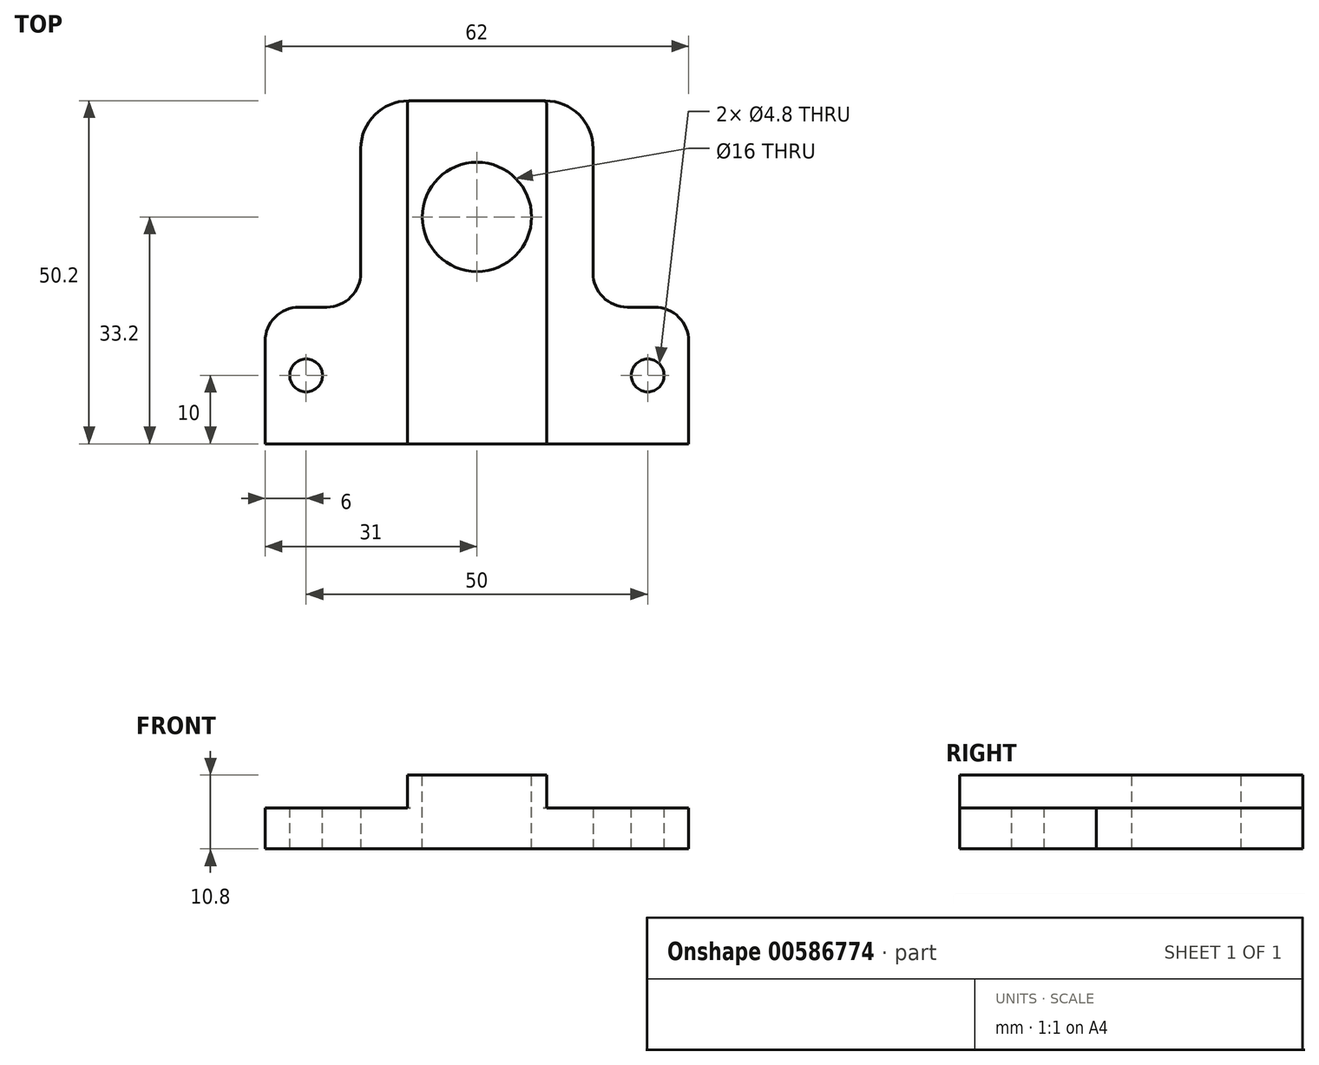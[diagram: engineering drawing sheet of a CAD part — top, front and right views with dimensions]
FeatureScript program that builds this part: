
annotation { "Feature Type Name" : "Feature", "Feature Type Description" : "" }
export const myFeature = defineFeature(function(context is Context, id is Id, definition is map)
    precondition{}
    {
        {
            var Q0;
            Q0=qCreatedBy(makeId("Top.planeOp"),FACE);
            var sketch = newSketch(context, id + "F0", { "sketchPlane" : qUnion([Q0])});
            skLineSegment(sketch, "E0.bottom", {"start": v(-31, 0) * mm, "end": v(31, 0) * mm});
            skLineSegment(sketch, "E0.top", {"start": v(-31, 20) * mm, "end": v(-17, 20) * mm});
            skLineSegment(sketch, "E0.left", {"start": v(-31, 0) * mm, "end": v(-31, 20) * mm});
            skLineSegment(sketch, "E0.right", {"start": v(31, 0) * mm, "end": v(31, 20) * mm});
            skLineSegment(sketch, "E1.top", {"start": v(-17, 50.2) * mm, "end": v(17, 50.2) * mm});
            skLineSegment(sketch, "E1.left", {"start": v(-17, 20) * mm, "end": v(-17, 50.2) * mm});
            skLineSegment(sketch, "E1.right", {"start": v(17, 20) * mm, "end": v(17, 50.2) * mm});
            skLineSegment(sketch, "E2.trimOffspring", {"start": v(17, 20) * mm, "end": v(31, 20) * mm});
            skPoint(sketch, "E3", {"position": v(0, 50.2) * mm});
            skPoint(sketch, "E4", {"position": v(0, 0) * mm});
            skSolve(sketch);
        }
        {
            var Q0;
            Q0 = qSketchRegion(id + "F0", true);
            extrude(context, id + "F1", {"entities" : qUnion([Q0]), "depth" : 6 * mm, "offsetDistance" : 25 * mm});
        }
        {
            var Q0;
            Q0=makeQuery(id+"F1.opExtrude","CAP_FACE",FACE,{"disambiguationData":[OSD([sQuery(id+"F0.wireOp",EDGE,"E0.bottom"),sQuery(id+"F0.wireOp",EDGE,"E0.top"),sQuery(id+"F0.wireOp",EDGE,"E0.left"),sQuery(id+"F0.wireOp",EDGE,"E0.right"),sQuery(id+"F0.wireOp",EDGE,"E1.top"),sQuery(id+"F0.wireOp",EDGE,"E1.left"),sQuery(id+"F0.wireOp",EDGE,"E1.right"),sQuery(id+"F0.wireOp",EDGE,"E2.trimOffspring")])],"isStart":false});
            var sketch = newSketch(context, id + "F2", { "sketchPlane" : qUnion([Q0])});
            skLineSegment(sketch, "E5.bottom", {"start": v(-10.2, 50.2) * mm, "end": v(10.2, 50.2) * mm});
            skLineSegment(sketch, "E5.top", {"start": v(-10.2, 0) * mm, "end": v(10.2, 0) * mm});
            skLineSegment(sketch, "E5.left", {"start": v(-10.2, 50.2) * mm, "end": v(-10.2, 0) * mm});
            skLineSegment(sketch, "E5.right", {"start": v(10.2, 50.2) * mm, "end": v(10.2, 0) * mm});
            skPoint(sketch, "E6", {"position": v(0, 50.2) * mm});
            skSolve(sketch);
        }
        {
            var Q0;
            Q0 = qSketchRegion(id + "F2", true);
            extrude(context, id + "F3", {"entities" : qUnion([Q0]), "operationType" : NewBodyOperationType.ADD, "depth" : 4.8 * mm, "offsetDistance" : 25 * mm});
        }
        {
            var Q0;
            Q0=makeQuery(id+"F3.opExtrude","CAP_FACE",FACE,{"disambiguationData":[OSD([sQuery(id+"F2.wireOp",EDGE,"E5.bottom"),sQuery(id+"F2.wireOp",EDGE,"E5.top"),sQuery(id+"F2.wireOp",EDGE,"E5.left"),sQuery(id+"F2.wireOp",EDGE,"E5.right")])],"isStart":false});
            var sketch = newSketch(context, id + "F4", { "sketchPlane" : qUnion([Q0])});
            skCircle(sketch, "E7", {"center": v(0, 33.2) * mm, "radius": 8 * mm});
            skSolve(sketch);
        }
        {
            var Q0;
            Q0 = qSketchRegion(id + "F4", true);
            extrude(context, id + "F5", {"entities" : qUnion([Q0]), "operationType" : NewBodyOperationType.REMOVE, "endBound" : BoundingType.THROUGH_ALL, "oppositeDirection" : true, "depth" : 25 * mm, "offsetDistance" : 25 * mm});
        }
        {
            var Q0;
            {var subQ0=sQuery(id+"F0.wireOp",EDGE,"E1.top");var subQ1=sQuery(id+"F0.wireOp",EDGE,"E0.left");var subQ2=sQuery(id+"F0.wireOp",EDGE,"E0.top");var subQ3=sQuery(id+"F0.wireOp",EDGE,"E0.bottom");var subQ4=sQuery(id+"F0.wireOp",EDGE,"E1.left");Q0=makeQuery(id+"F3.boolean.opBoolean","SPLIT",FACE,{"disambiguationData":[TD([makeQuery(id+"F1.opExtrude","SWEPT_FACE",FACE,{"disambiguationData":[OSD([subQ2])]})])],"derivedFrom":makeQuery(id+"F1.opExtrude","CAP_FACE",FACE,{"disambiguationData":[OSD([subQ3,subQ2,subQ1,sQuery(id+"F0.wireOp",EDGE,"E0.right"),subQ0,subQ4,sQuery(id+"F0.wireOp",EDGE,"E1.right"),sQuery(id+"F0.wireOp",EDGE,"E2.trimOffspring")])],"isStart":false})});}
            var sketch = newSketch(context, id + "F6", { "sketchPlane" : qUnion([Q0])});
            skCircle(sketch, "E8", {"center": v(-25, 10) * mm, "radius": 2.4 * mm});
            skCircle(sketch, "E9.MirrorC", {"center": v(25, 10) * mm, "radius": 2.4 * mm});
            skSolve(sketch);
        }
        {
            var Q0;
            Q0 = qSketchRegion(id + "F6", true);
            extrude(context, id + "F7", {"entities" : qUnion([Q0]), "operationType" : NewBodyOperationType.REMOVE, "endBound" : BoundingType.THROUGH_ALL, "oppositeDirection" : true, "depth" : 25 * mm, "offsetDistance" : 25 * mm});
        }
        {
            var Q0;
            Q0=makeQuery(id+"F1.opExtrude","SWEPT_EDGE",EDGE,{"disambiguationData":[OSD([sQuery(id+"F0.wireOp",EDGE,"E1.top"),sQuery(id+"F0.wireOp",EDGE,"E1.right")])]});
            var Q1;
            Q1=makeQuery(id+"F1.opExtrude","SWEPT_EDGE",EDGE,{"disambiguationData":[OSD([sQuery(id+"F0.wireOp",EDGE,"E1.top"),sQuery(id+"F0.wireOp",EDGE,"E1.left")])]});
            fillet(context, id + "F8", {"entities" : qUnion([Q0, Q1]), "radius" : 7 * mm, "tangentPropagation" : true, "allowEdgeOverflow" : false});
        }
        {
            var Q0;
            Q0=makeQuery(id+"F1.opExtrude","SWEPT_EDGE",EDGE,{"disambiguationData":[OSD([sQuery(id+"F0.wireOp",EDGE,"E0.top"),sQuery(id+"F0.wireOp",EDGE,"E0.left")])]});
            var Q1;
            Q1=makeQuery(id+"F1.opExtrude","SWEPT_EDGE",EDGE,{"disambiguationData":[OSD([sQuery(id+"F0.wireOp",EDGE,"E0.right"),sQuery(id+"F0.wireOp",EDGE,"E2.trimOffspring")])]});
            var Q2;
            Q2=makeQuery(id+"F1.opExtrude","SWEPT_EDGE",EDGE,{"disambiguationData":[OSD([sQuery(id+"F0.wireOp",EDGE,"E1.right"),sQuery(id+"F0.wireOp",EDGE,"E2.trimOffspring")])]});
            var Q3;
            Q3=makeQuery(id+"F1.opExtrude","SWEPT_EDGE",EDGE,{"disambiguationData":[OSD([sQuery(id+"F0.wireOp",EDGE,"E0.top"),sQuery(id+"F0.wireOp",EDGE,"E1.left")])]});
            fillet(context, id + "F9", {"entities" : qUnion([Q0, Q1, Q2, Q3]), "radius" : 5 * mm, "tangentPropagation" : true, "allowEdgeOverflow" : false});
        }
        {
            var Q0;
            Q0=makeQuery(id+"F8.opFillet","BLEND_EDGE",EDGE,{"blendedFrom":[makeQuery(id+"F1.opExtrude","SWEPT_EDGE",EDGE,{"disambiguationData":[OSD([sQuery(id+"F0.wireOp",EDGE,"E1.top"),sQuery(id+"F0.wireOp",EDGE,"E1.right")])]}),makeQuery(id+"F3.opExtrude","SWEPT_FACE",FACE,{"disambiguationData":[OSD([sQuery(id+"F2.wireOp",EDGE,"E5.right")])]})],"blendedInto":[makeQuery(id+"F3.opExtrude","SWEPT_FACE",FACE,{"disambiguationData":[OSD([sQuery(id+"F2.wireOp",EDGE,"E5.right")])]})]});
            var Q1;
            Q1=makeQuery(id+"F8.opFillet","BLEND_EDGE",EDGE,{"blendedFrom":[makeQuery(id+"F1.opExtrude","SWEPT_EDGE",EDGE,{"disambiguationData":[OSD([sQuery(id+"F0.wireOp",EDGE,"E1.top"),sQuery(id+"F0.wireOp",EDGE,"E1.left")])]}),makeQuery(id+"F3.opExtrude","SWEPT_FACE",FACE,{"disambiguationData":[OSD([sQuery(id+"F2.wireOp",EDGE,"E5.left")])]})],"blendedInto":[makeQuery(id+"F3.opExtrude","SWEPT_FACE",FACE,{"disambiguationData":[OSD([sQuery(id+"F2.wireOp",EDGE,"E5.left")])]})]});
            fillet(context, id + "F10", {"entities" : qUnion([Q0, Q1]), "radius" : .5 * mm, "tangentPropagation" : true, "allowEdgeOverflow" : false});
        }
    });
